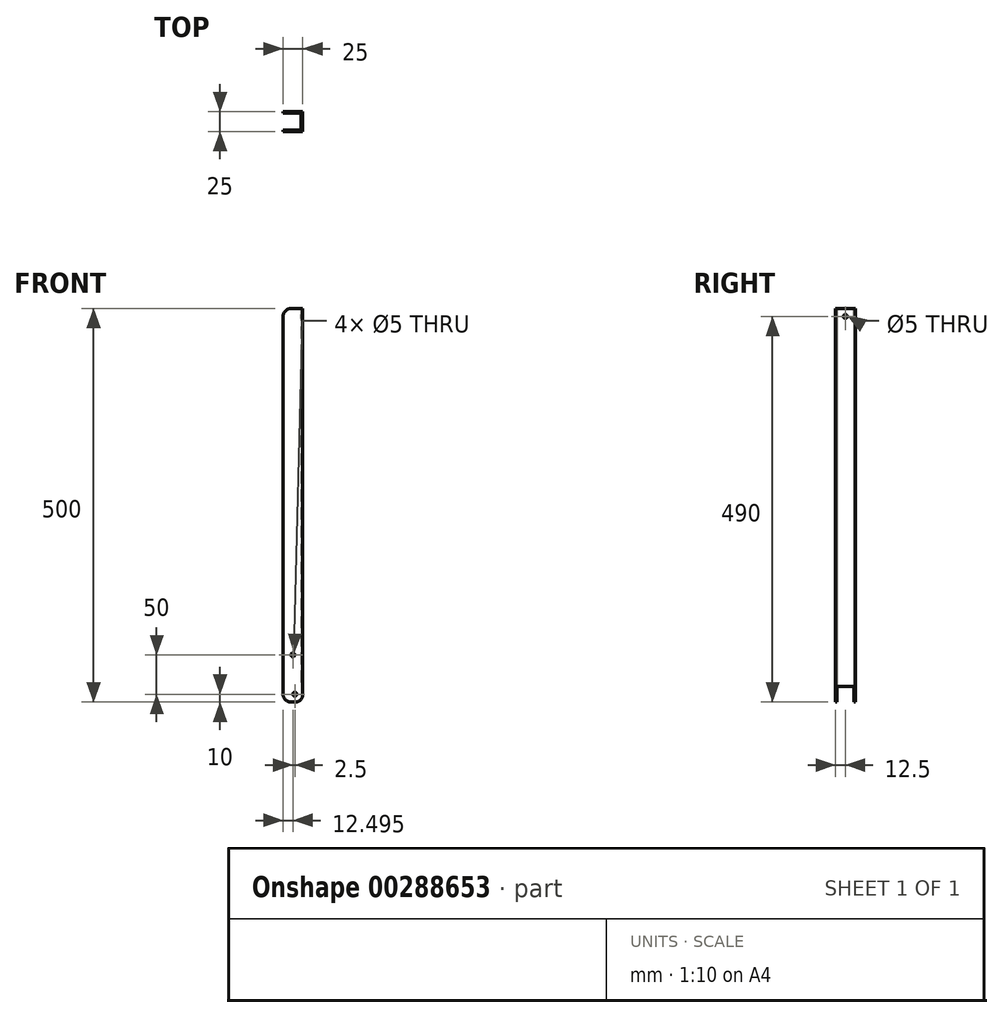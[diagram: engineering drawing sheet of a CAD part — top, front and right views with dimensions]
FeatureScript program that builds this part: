
annotation { "Feature Type Name" : "Feature", "Feature Type Description" : "" }
export const myFeature = defineFeature(function(context is Context, id is Id, definition is map)
    precondition{}
    {
        {
            var Q0;
            Q0=qCreatedBy(makeId("Top.planeOp"),FACE);
            var sketch = newSketch(context, id + "F0", { "sketchPlane" : qUnion([Q0])});
            skLineSegment(sketch, "E0", {"start": v(-46.83, -43.4) * mm, "end": v(-21.83, -43.4) * mm});
            skLineSegment(sketch, "E1", {"start": v(-21.83, -43.4) * mm, "end": v(-21.83, -18.4) * mm});
            skLineSegment(sketch, "E2", {"start": v(-21.83, -18.4) * mm, "end": v(-46.83, -18.4) * mm});
            skLineSegment(sketch, "E3", {"start": v(-46.83, -18.4) * mm, "end": v(-46.83, -20.4) * mm});
            skLineSegment(sketch, "E4", {"start": v(-46.83, -20.4) * mm, "end": v(-23.83, -20.4) * mm});
            skLineSegment(sketch, "E5", {"start": v(-23.83, -20.4) * mm, "end": v(-23.83, -41.4) * mm});
            skLineSegment(sketch, "E6", {"start": v(-23.83, -41.4) * mm, "end": v(-46.83, -41.4) * mm});
            skLineSegment(sketch, "E7", {"start": v(-46.83, -41.4) * mm, "end": v(-46.83, -43.4) * mm});
            skSolve(sketch);
        }
        {
            var Q0;
            Q0=makeQuery(id+"F0.imprint","IMPRINT",FACE,{"disambiguationData":[TD([[makeQuery(id+"F0.imprint","IMPRINT",EDGE,{"derivedFrom":sQuery(id+"F0.wireOp",EDGE,"E0")}),1.0]])]});
            extrude(context, id + "F1", {"entities" : qUnion([Q0]), "depth" : 500 * mm});
        }
        {
            var Q0;
            Q0=makeQuery(id+"F1.opExtrude","CAP_FACE",FACE,{"disambiguationData":[OSD([sQuery(id+"F0.wireOp",EDGE,"E0"),sQuery(id+"F0.wireOp",EDGE,"E1"),sQuery(id+"F0.wireOp",EDGE,"E2"),sQuery(id+"F0.wireOp",EDGE,"E3"),sQuery(id+"F0.wireOp",EDGE,"E4"),sQuery(id+"F0.wireOp",EDGE,"E5"),sQuery(id+"F0.wireOp",EDGE,"E6"),sQuery(id+"F0.wireOp",EDGE,"E7")])],"isStart":true});
            var sketch = newSketch(context, id + "F2", { "sketchPlane" : qUnion([Q0])});
            skLineSegment(sketch, "E8.bottom", {"start": v(-23.83, 41.4) * mm, "end": v(-21.83, 41.4) * mm});
            skLineSegment(sketch, "E8.top", {"start": v(-23.83, 20.4) * mm, "end": v(-21.83, 20.4) * mm});
            skLineSegment(sketch, "E8.left", {"start": v(-23.83, 41.4) * mm, "end": v(-23.83, 20.4) * mm});
            skLineSegment(sketch, "E8.right", {"start": v(-21.83, 41.4) * mm, "end": v(-21.83, 20.4) * mm});
            skSolve(sketch);
        }
        {
            var Q0;
            Q0=makeQuery(id+"F2.imprint","IMPRINT",FACE,{"disambiguationData":[TD([[makeQuery(id+"F2.imprint","IMPRINT",EDGE,{"derivedFrom":sQuery(id+"F2.wireOp",EDGE,"E8.bottom")}),-1.0]])]});
            extrude(context, id + "F3", {"entities" : qUnion([Q0]), "operationType" : NewBodyOperationType.REMOVE, "oppositeDirection" : true, "depth" : 20 * mm});
        }
        {
            var Q0;
            Q0=makeQuery(id+"F1.opExtrude","SWEPT_FACE",FACE,{"disambiguationData":[OSD([sQuery(id+"F0.wireOp",EDGE,"E0")])]});
            var sketch = newSketch(context, id + "F4", { "sketchPlane" : qUnion([Q0])});
            skCircle(sketch, "E9", {"center": v(-31.83, 10) * mm, "radius": 2.5 * mm});
            skSolve(sketch);
        }
        {
            var Q0;
            Q0=makeQuery(id+"F4.imprint","IMPRINT",FACE,{"disambiguationData":[TD([[makeQuery(id+"F4.imprint","IMPRINT",EDGE,{"derivedFrom":sQuery(id+"F4.wireOp",EDGE,"E9")}),1.0]])]});
            extrude(context, id + "F5", {"entities" : qUnion([Q0]), "operationType" : NewBodyOperationType.REMOVE, "oppositeDirection" : true, "depth" : 25 * mm});
        }
        {
            var Q0;
            Q0=makeQuery(id+"F1.opExtrude","CAP_EDGE",EDGE,{"disambiguationData":[OSD([sQuery(id+"F0.wireOp",EDGE,"E3")])],"isStart":true});
            var Q1;
            Q1=makeQuery(id+"F1.opExtrude","CAP_EDGE",EDGE,{"disambiguationData":[OSD([sQuery(id+"F0.wireOp",EDGE,"E7")])],"isStart":true});
            var Q2;
            Q2=makeQuery(id+"F1.opExtrude","CAP_EDGE",EDGE,{"disambiguationData":[OSD([sQuery(id+"F0.wireOp",EDGE,"E7")])],"isStart":false});
            var Q3;
            Q3=makeQuery(id+"F1.opExtrude","CAP_EDGE",EDGE,{"disambiguationData":[OSD([sQuery(id+"F0.wireOp",EDGE,"E3")])],"isStart":false});
            var Q4;
            {var subQ1=sQuery(id+"F0.wireOp",EDGE,"E1");var subQ2=sQuery(id+"F0.wireOp",EDGE,"E0");Q4=makeQuery(id+"F3.boolean.opBoolean","SPLIT",EDGE,{"disambiguationData":[TD([makeQuery(id+"F1.opExtrude","SWEPT_FACE",FACE,{"disambiguationData":[OSD([subQ2])]})])],"derivedFrom":makeQuery(id+"F1.opExtrude","CAP_EDGE",EDGE,{"disambiguationData":[OSD([subQ1])],"isStart":true})});}
            var Q5;
            {var subQ0=sQuery(id+"F0.wireOp",EDGE,"E2");var subQ1=sQuery(id+"F0.wireOp",EDGE,"E1");Q5=makeQuery(id+"F3.boolean.opBoolean","SPLIT",EDGE,{"disambiguationData":[TD([makeQuery(id+"F1.opExtrude","SWEPT_FACE",FACE,{"disambiguationData":[OSD([subQ0])]})])],"derivedFrom":makeQuery(id+"F1.opExtrude","CAP_EDGE",EDGE,{"disambiguationData":[OSD([subQ1])],"isStart":true})});}
            fillet(context, id + "F6", {"entities" : qUnion([Q0, Q1, Q2, Q3, Q4, Q5]), "radius" : 10 * mm, "tangentPropagation" : true, "allowEdgeOverflow" : false});
        }
        {
            var Q0;
            Q0=makeQuery(id+"F1.opExtrude","SWEPT_FACE",FACE,{"disambiguationData":[OSD([sQuery(id+"F0.wireOp",EDGE,"E1")])]});
            var sketch = newSketch(context, id + "F7", { "sketchPlane" : qUnion([Q0])});
            skCircle(sketch, "E10", {"center": v(-30.9, 490) * mm, "radius": 2.5 * mm});
            skPoint(sketch, "E10.centerSnap0", {"position": v(-30.9, 500) * mm});
            skSolve(sketch);
        }
        {
            var Q0;
            Q0=makeQuery(id+"F7.imprint","IMPRINT",FACE,{"disambiguationData":[TD([[makeQuery(id+"F7.imprint","IMPRINT",EDGE,{"derivedFrom":sQuery(id+"F7.wireOp",EDGE,"E10")}),1.0]])]});
            extrude(context, id + "F8", {"entities" : qUnion([Q0]), "operationType" : NewBodyOperationType.REMOVE, "oppositeDirection" : true, "depth" : 25 * mm});
        }
        {
            var Q0;
            Q0=makeQuery(id+"F1.opExtrude","SWEPT_FACE",FACE,{"disambiguationData":[OSD([sQuery(id+"F0.wireOp",EDGE,"E0")])]});
            var sketch = newSketch(context, id + "F9", { "sketchPlane" : qUnion([Q0])});
            skCircle(sketch, "E11", {"center": v(-34.33, 60) * mm, "radius": 2.5 * mm});
            skSolve(sketch);
        }
        {
            var Q0;
            Q0=makeQuery(id+"F9.imprint","IMPRINT",FACE,{"disambiguationData":[TD([[makeQuery(id+"F9.imprint","IMPRINT",EDGE,{"derivedFrom":sQuery(id+"F9.wireOp",EDGE,"E11")}),1.0]])]});
            extrude(context, id + "F10", {"entities" : qUnion([Q0]), "operationType" : NewBodyOperationType.REMOVE, "oppositeDirection" : true, "depth" : 25 * mm, "offsetDistance" : 25 * mm});
        }
    });
